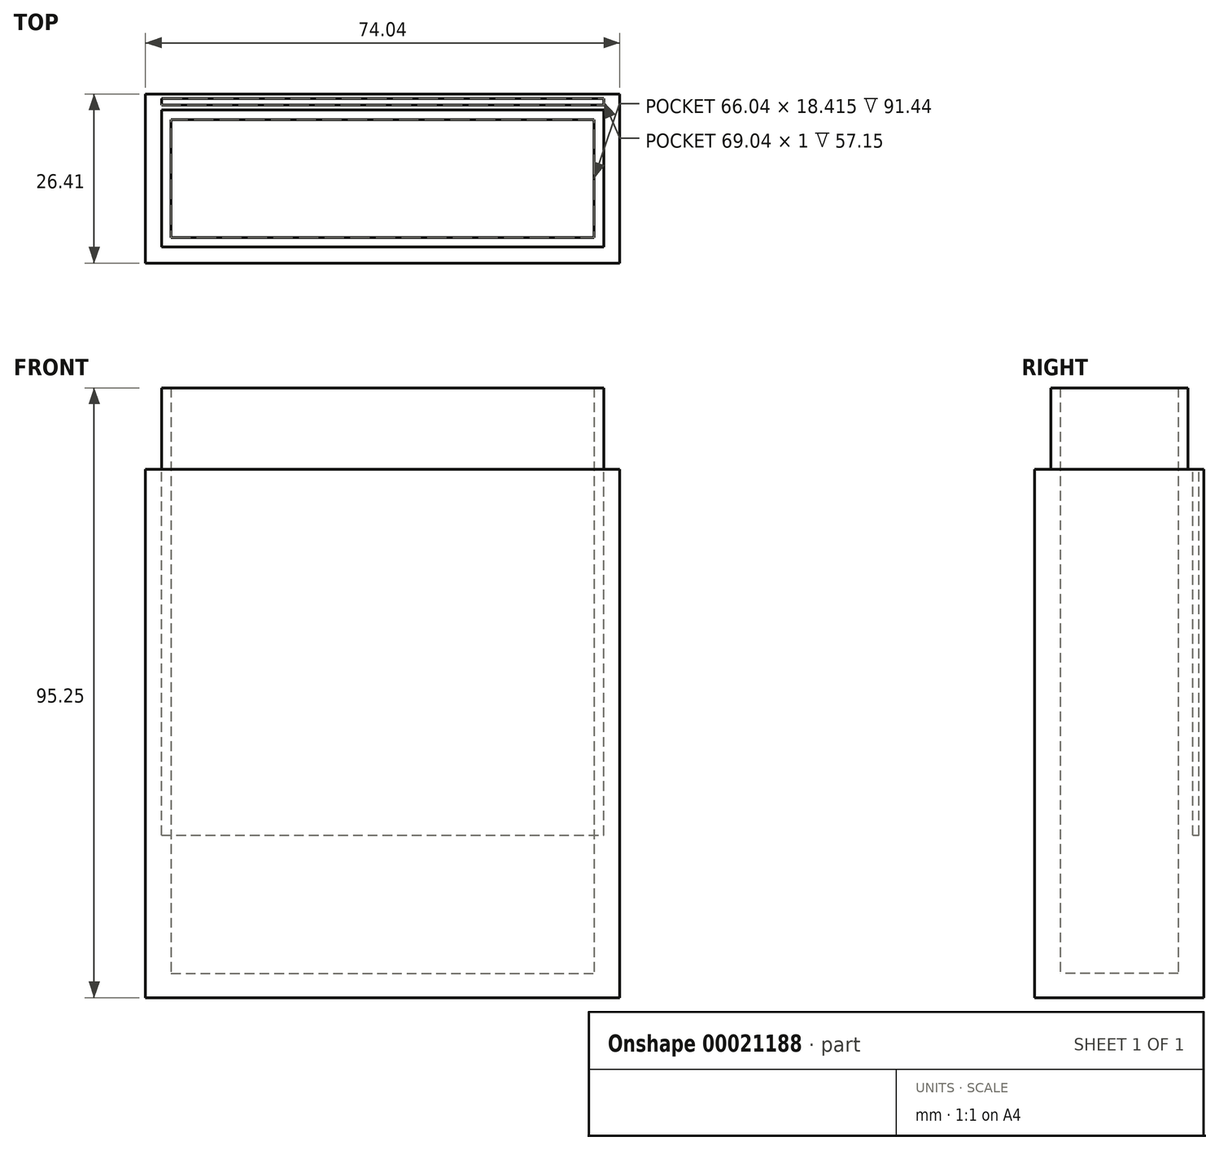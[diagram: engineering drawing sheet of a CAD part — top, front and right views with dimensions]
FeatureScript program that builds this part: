
annotation { "Feature Type Name" : "Feature", "Feature Type Description" : "" }
export const myFeature = defineFeature(function(context is Context, id is Id, definition is map)
    precondition{}
    {
        {
            var Q0;
            Q0=qCreatedBy(makeId("Top.planeOp"),FACE);
            var sketch = newSketch(context, id + "F0", { "sketchPlane" : qUnion([Q0])});
            skLineSegment(sketch, "E0.bottom", {"start": v(0, 0) * mm, "end": v(66.04, 0) * mm});
            skLineSegment(sketch, "E0.top", {"start": v(0, -18.42) * mm, "end": v(66.04, -18.42) * mm});
            skLineSegment(sketch, "E0.left", {"start": v(0, 0) * mm, "end": v(0, -18.42) * mm});
            skLineSegment(sketch, "E0.right", {"start": v(66.04, 0) * mm, "end": v(66.04, -18.42) * mm});
            skLineSegment(sketch, "E1.bottom", {"start": v(-4, 4) * mm, "end": v(70.04, 4) * mm});
            skLineSegment(sketch, "E1.top", {"start": v(-4, -22.42) * mm, "end": v(70.04, -22.42) * mm});
            skLineSegment(sketch, "E1.left", {"start": v(-4, 4) * mm, "end": v(-4, -22.42) * mm});
            skLineSegment(sketch, "E1.right", {"start": v(70.04, 4) * mm, "end": v(70.04, -22.42) * mm});
            skLineSegment(sketch, "E2", {"start": v(0, 0) * mm, "end": v(0, 4) * mm});
            skLineSegment(sketch, "E3", {"start": v(0, 0) * mm, "end": v(-4, 0) * mm});
            skLineSegment(sketch, "E4", {"start": v(-4, 0) * mm, "end": v(0, 0) * mm});
            skLineSegment(sketch, "E5", {"start": v(66.04, -18.42) * mm, "end": v(66.04, -22.42) * mm});
            skLineSegment(sketch, "E6", {"start": v(66.04, -18.42) * mm, "end": v(70.04, -18.42) * mm});
            skSolve(sketch);
        }
        {
            var Q0;
            {var subQ1=sQuery(id+"F0.wireOp",EDGE,"E2");Q0=makeQuery(id+"F0.imprint","IMPRINT",FACE,{"disambiguationData":[TD([[makeQuery(id+"F0.imprint","IMPRINT",EDGE,{"derivedFrom":subQ1}),1.0]])]});}
            var Q1;
            Q1=makeQuery(id+"F0.imprint","IMPRINT",FACE,{"disambiguationData":[TD([[makeQuery(id+"F0.imprint","IMPRINT",EDGE,{"derivedFrom":sQuery(id+"F0.wireOp",EDGE,"E0.bottom")}),1.0]])]});
            var Q2;
            Q2=makeQuery(id+"F0.imprint","IMPRINT",FACE,{"disambiguationData":[TD([[makeQuery(id+"F0.imprint","IMPRINT",EDGE,{"derivedFrom":sQuery(id+"F0.wireOp",EDGE,"E0.top")}),-1.0]])]});
            var Q3;
            {var subQ1=sQuery(id+"F0.wireOp",EDGE,"E5");Q3=makeQuery(id+"F0.imprint","IMPRINT",FACE,{"disambiguationData":[TD([[makeQuery(id+"F0.imprint","IMPRINT",EDGE,{"derivedFrom":subQ1}),1.0]])]});}
            var Q4;
            Q4 = qSketchRegion(id + "F2", true);
            extrude(context, id + "F1", {"entities" : qUnion([Q0, Q1, Q2, Q3, Q4]), "depth" : 78.74 * mm});
        }
        {
            var Q0;
            Q0=makeQuery(id+"F1.opExtrude","CAP_FACE",FACE,{"disambiguationData":[OSD([sQuery(id+"F0.wireOp",EDGE,"E0.bottom"),sQuery(id+"F0.wireOp",EDGE,"E0.top"),sQuery(id+"F0.wireOp",EDGE,"E0.left"),sQuery(id+"F0.wireOp",EDGE,"E0.right"),sQuery(id+"F0.wireOp",EDGE,"E1.bottom"),sQuery(id+"F0.wireOp",EDGE,"E1.top"),sQuery(id+"F0.wireOp",EDGE,"E1.left"),sQuery(id+"F0.wireOp",EDGE,"E1.right")])],"isStart":false});
            var sketch = newSketch(context, id + "F2", { "sketchPlane" : qUnion([Q0])});
            skLineSegment(sketch, "E7", {"start": v(0, 0) * mm, "end": v(-1.5, 0) * mm});
            skLineSegment(sketch, "E8", {"start": v(0, 0) * mm, "end": v(0, 1.5) * mm});
            skLineSegment(sketch, "E9", {"start": v(66.04, -18.42) * mm, "end": v(66.04, -19.92) * mm});
            skLineSegment(sketch, "E10", {"start": v(66.04, -18.42) * mm, "end": v(67.54, -18.42) * mm});
            skLineSegment(sketch, "E11.bottom", {"start": v(-1.5, 1.5) * mm, "end": v(67.54, 1.5) * mm});
            skLineSegment(sketch, "E11.top", {"start": v(-1.5, -19.92) * mm, "end": v(67.54, -19.92) * mm});
            skLineSegment(sketch, "E11.left", {"start": v(-1.5, 1.5) * mm, "end": v(-1.5, -19.92) * mm});
            skLineSegment(sketch, "E11.right", {"start": v(67.54, 1.5) * mm, "end": v(67.54, -19.92) * mm});
            skSolve(sketch);
        }
        {
            var Q0;
            {var subQ4=sQuery(id+"F2.wireOp",EDGE,"E8");Q0=makeQuery(id+"F2.imprint","IMPRINT",FACE,{"disambiguationData":[TD([[makeQuery(id+"F2.imprint","IMPRINT",EDGE,{"derivedFrom":subQ4}),-1.0]])]});}
            var Q1;
            {var subQ3=sQuery(id+"F2.wireOp",EDGE,"E7");Q1=makeQuery(id+"F2.imprint","IMPRINT",FACE,{"disambiguationData":[TD([[makeQuery(id+"F2.imprint","IMPRINT",EDGE,{"derivedFrom":subQ3}),-1.0]])]});}
            var Q2;
            {var subQ3=sQuery(id+"F2.wireOp",EDGE,"E7");Q2=makeQuery(id+"F2.imprint","IMPRINT",FACE,{"disambiguationData":[TD([[makeQuery(id+"F2.imprint","IMPRINT",EDGE,{"derivedFrom":subQ3}),1.0]])]});}
            var Q3;
            {var subQ4=sQuery(id+"F2.wireOp",EDGE,"E9");Q3=makeQuery(id+"F2.imprint","IMPRINT",FACE,{"disambiguationData":[TD([[makeQuery(id+"F2.imprint","IMPRINT",EDGE,{"derivedFrom":subQ4}),1.0]])]});}
            extrude(context, id + "F3", {"entities" : qUnion([Q0, Q1, Q2, Q3]), "operationType" : NewBodyOperationType.ADD, "depth" : 12.7 * mm});
        }
        {
            var Q0;
            Q0=makeQuery(id+"F1.opExtrude","CAP_FACE",FACE,{"disambiguationData":[OSD([sQuery(id+"F0.wireOp",EDGE,"E0.bottom"),sQuery(id+"F0.wireOp",EDGE,"E0.top"),sQuery(id+"F0.wireOp",EDGE,"E0.left"),sQuery(id+"F0.wireOp",EDGE,"E0.right"),sQuery(id+"F0.wireOp",EDGE,"E1.bottom"),sQuery(id+"F0.wireOp",EDGE,"E1.top"),sQuery(id+"F0.wireOp",EDGE,"E1.left"),sQuery(id+"F0.wireOp",EDGE,"E1.right")])],"isStart":true});
            var sketch = newSketch(context, id + "F4", { "sketchPlane" : qUnion([Q0])});
            skLineSegment(sketch, "E12.bottom", {"start": v(-4, 22.42) * mm, "end": v(70.04, 22.42) * mm});
            skLineSegment(sketch, "E12.top", {"start": v(-4, -4) * mm, "end": v(70.04, -4) * mm});
            skLineSegment(sketch, "E12.left", {"start": v(-4, 22.42) * mm, "end": v(-4, -4) * mm});
            skLineSegment(sketch, "E12.right", {"start": v(70.04, 22.42) * mm, "end": v(70.04, -4) * mm});
            skSolve(sketch);
        }
        {
            var Q0;
            Q0=makeQuery(id+"F4.imprint","IMPRINT",FACE,{"disambiguationData":[TD([[makeQuery(id+"F4.imprint","IMPRINT",EDGE,{"derivedFrom":makeQuery(id+"F1.opExtrude","CAP_EDGE",EDGE,{"disambiguationData":[OSD([sQuery(id+"F0.wireOp",EDGE,"E0.bottom")])],"isStart":true})}),1.0]])]});
            var Q1;
            Q1=makeQuery(id+"F4.imprint","IMPRINT",FACE,{"disambiguationData":[TD([[makeQuery(id+"F4.imprint","IMPRINT",EDGE,{"derivedFrom":sQuery(id+"F4.wireOp",EDGE,"E12.bottom")}),-1.0]])]});
            extrude(context, id + "F5", {"entities" : qUnion([Q0, Q1]), "operationType" : NewBodyOperationType.ADD, "depth" : 3.8 * mm});
        }
        {
            var Q0;
            Q0=makeQuery(id+"F1.opExtrude","CAP_FACE",FACE,{"disambiguationData":[OSD([sQuery(id+"F0.wireOp",EDGE,"E0.bottom"),sQuery(id+"F0.wireOp",EDGE,"E0.top"),sQuery(id+"F0.wireOp",EDGE,"E0.left"),sQuery(id+"F0.wireOp",EDGE,"E0.right"),sQuery(id+"F0.wireOp",EDGE,"E1.bottom"),sQuery(id+"F0.wireOp",EDGE,"E1.top"),sQuery(id+"F0.wireOp",EDGE,"E1.left"),sQuery(id+"F0.wireOp",EDGE,"E1.right")])],"isStart":false});
            var sketch = newSketch(context, id + "F6", { "sketchPlane" : qUnion([Q0])});
            skLineSegment(sketch, "E13.bottom", {"start": v(-1.5, 2.25) * mm, "end": v(67.54, 2.25) * mm});
            skLineSegment(sketch, "E13.top", {"start": v(-1.5, 3.25) * mm, "end": v(67.54, 3.25) * mm});
            skLineSegment(sketch, "E13.left", {"start": v(-1.5, 2.25) * mm, "end": v(-1.5, 3.25) * mm});
            skLineSegment(sketch, "E13.right", {"start": v(67.54, 2.25) * mm, "end": v(67.54, 3.25) * mm});
            skLineSegment(sketch, "E14", {"start": v(-1.5, 2.25) * mm, "end": v(-1.5, 1.5) * mm});
            skSolve(sketch);
        }
        {
            var Q0;
            Q0=makeQuery(id+"F6.imprint","IMPRINT",FACE,{"disambiguationData":[TD([[makeQuery(id+"F6.imprint","IMPRINT",EDGE,{"derivedFrom":sQuery(id+"F6.wireOp",EDGE,"23d8d84a-2447-41a7-aefd-b34db744feb5.bottom")}),1.0]])]});
            var Q1;
            Q1=makeQuery(id+"F6.imprint","IMPRINT",FACE,{"disambiguationData":[TD([[makeQuery(id+"F6.imprint","IMPRINT",EDGE,{"derivedFrom":sQuery(id+"F6.wireOp",EDGE,"E13.bottom")}),1.0]])]});
            extrude(context, id + "F7", {"entities" : qUnion([Q0, Q1]), "operationType" : NewBodyOperationType.REMOVE, "oppositeDirection" : true, "depth" : 57.15 * mm});
        }
    });
